# Revit family: Sink-Vessel-Lavatory-KOHLER-Brazn-K-EX21060T
name_source: partatom
category: Plumbing Fixtures
units: mm (PartAtom-declared; Revit-internal decimal feet)

## family parameters
Cut with Voids When Loaded = No
Host = Face
OmniClass Number = 23.31.13.00
OmniClass Title = Sinks
Part Type = Normal
Room Calculation Point = No
Round Connector Dimension = Use Diameter
Shared = No

## types (6) — shared parameters
ADA Compliant = No
Assembly Code = D2010400
CW Connection = No
Cold Water Inlet = Cold Water Inlet
Date Modified = 12/21/2022
Default Elevation = 36"
Drain Included = Yes
HW Connection = No
Height = 7"
Hot Water Inlet = Hot Water Inlet
Length = 23"
Manufacturer = Kohler Co.
Master Format 2014 = 22 41 16
Master Format 2014 Name = Residential Lavatories and Sinks
Material = Vitreous China
Product Name = Brazn
URL = http://www.kohler.com.cn
Vent Connection = No
Waste Connection = Yes
Waste Water Outlet = Waste Water Outlet
WaterSense Certified = No
Width = 16"

## per-type parameters (varying)
| type | Description | Finish | Model | Product Documentation Link | Product Page URL | Type |
| 0-White | Lingyue rectangular stylish washbasin | Kohler-Vitreous_China-0-White | K-EX21060T-0 | https://files.kohler.com.cn | https://www.kohler.com.cn | 1 |
| HB1-Honed Black | Lingyue rectangular stylish washbasin | Kohler-Vitreous_China-HB1-Honed_Black | K-EX21060T-HB1 | https://files.kohler.com.cn |  | 2 |
| With Elle, 0-White | Rectangle Vessel Without Deck | Kohler-Vitreous_China-0-White | K-EX21060T-AE1-0 |  |  | 3 |
| With Nahu, 0-White | Rectangle Vessel Without Deck | Kohler-Vitreous_China-0-White | K-EX21060T-AE2-0 |  |  | 4 |
| With Kumari, 0-White | Rectangle Vessel Without Deck | Kohler-Vitreous_China-0-White | K-EX21060T-AE3-0 |  |  | 5 |
| With Ziling, 0-White | Rectangle Vessel Without Deck | Kohler-Vitreous_China-0-White | K-EX21060T-AE4-0 |  |  | 6 |

## geometry (parser evidence)
native form markers: Sweep x4
no freeform markers — native parametric forms only
